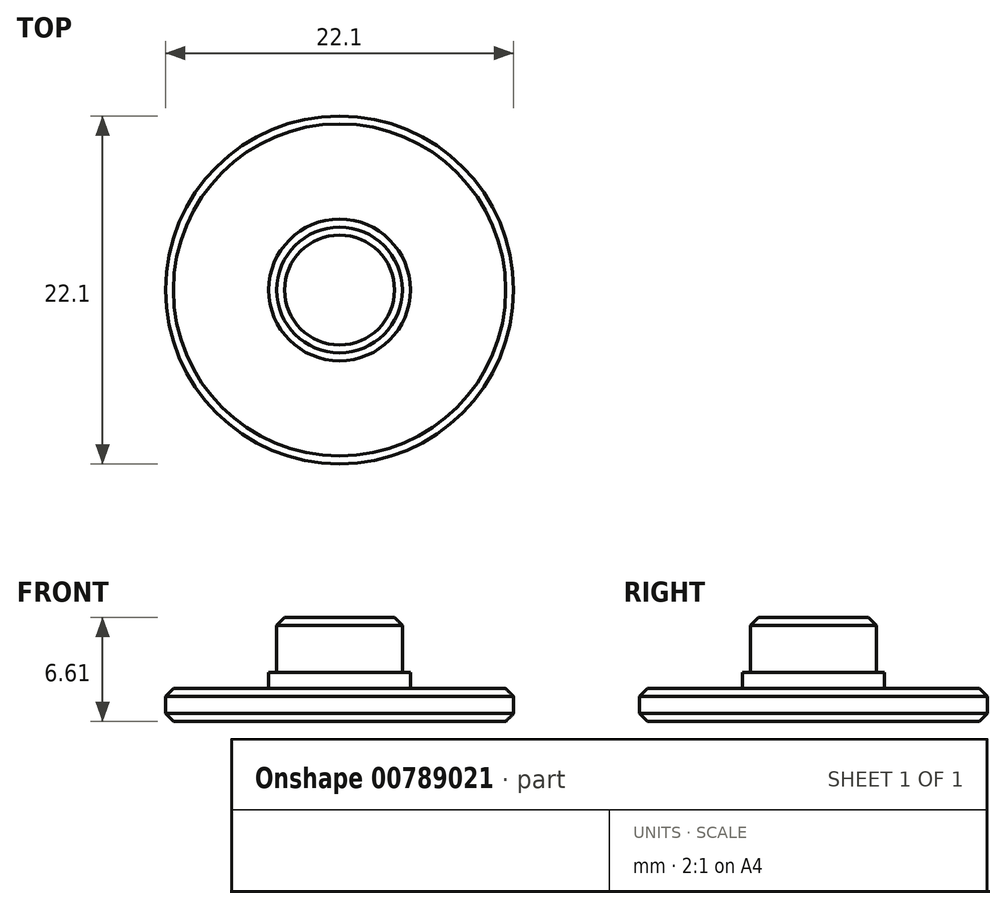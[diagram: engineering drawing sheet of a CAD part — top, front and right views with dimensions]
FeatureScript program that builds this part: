
annotation { "Feature Type Name" : "Feature", "Feature Type Description" : "" }
export const myFeature = defineFeature(function(context is Context, id is Id, definition is map)
    precondition{}
    {
        {
            var Q0;
            Q0=qCreatedBy(makeId("Top.planeOp"),FACE);
            var sketch = newSketch(context, id + "F0", { "sketchPlane" : qUnion([Q0])});
            skCircle(sketch, "E0", {"center": v(0, 0) * mm, "radius": 11.05 * mm});
            skSolve(sketch);
        }
        {
            var Q0;
            Q0=qSketchRegion(id+"F0",true);
            extrude(context, id + "F1", {"entities" : qUnion([Q0]), "depth" : 2.1 * mm, "offsetDistance" : 25 * mm});
        }
        {
            var Q0;
            Q0=makeQuery(id+"F1.opExtrude","CAP_FACE",FACE,{"disambiguationData":[OSD([sQuery(id+"F0.wireOp",EDGE,"E0")])],"isStart":false});
            var sketch = newSketch(context, id + "F2", { "sketchPlane" : qUnion([Q0])});
            skCircle(sketch, "E1", {"center": v(0, 0) * mm, "radius": 4.5 * mm});
            skSolve(sketch);
        }
        {
            var Q0;
            Q0=makeQuery(id+"F2.imprint","IMPRINT",FACE,{"disambiguationData":[TD([[makeQuery(id+"F2.imprint","IMPRINT",EDGE,{"derivedFrom":sQuery(id+"F2.wireOp",EDGE,"E1")}),1.0]])]});
            extrude(context, id + "F3", {"entities" : qUnion([Q0]), "operationType" : NewBodyOperationType.ADD, "depth" : 1.01 * mm, "offsetDistance" : 25 * mm});
        }
        {
            var Q0;
            Q0=makeQuery(id+"F3.opExtrude","CAP_FACE",FACE,{"disambiguationData":[OSD([sQuery(id+"F2.wireOp",EDGE,"E1")])],"isStart":false});
            var sketch = newSketch(context, id + "F4", { "sketchPlane" : qUnion([Q0])});
            skCircle(sketch, "E2", {"center": v(0, 0) * mm, "radius": 4 * mm});
            skSolve(sketch);
        }
        {
            var Q0;
            Q0=makeQuery(id+"F4.imprint","IMPRINT",FACE,{"disambiguationData":[TD([[makeQuery(id+"F4.imprint","IMPRINT",EDGE,{"derivedFrom":sQuery(id+"F4.wireOp",EDGE,"E2")}),1.0]])]});
            extrude(context, id + "F5", {"entities" : qUnion([Q0]), "operationType" : NewBodyOperationType.ADD, "depth" : 3.5 * mm, "offsetDistance" : 25 * mm});
        }
        {
            var Q0;
            Q0=makeQuery(id+"F1.opExtrude","CAP_EDGE",EDGE,{"disambiguationData":[OSD([sQuery(id+"F0.wireOp",EDGE,"E0")])],"isStart":false});
            var Q1;
            Q1=makeQuery(id+"F5.opExtrude","CAP_FACE",FACE,{"disambiguationData":[OSD([sQuery(id+"F4.wireOp",EDGE,"E2")])],"isStart":false});
            var Q2;
            Q2=makeQuery(id+"F1.opExtrude","CAP_FACE",FACE,{"disambiguationData":[OSD([sQuery(id+"F0.wireOp",EDGE,"E0")])],"isStart":true});
            chamfer(context, id + "F6", {"entities" : qUnion([Q0, Q1, Q2]), "width" : .5 * mm, "tangentPropagation" : true});
        }
    });
